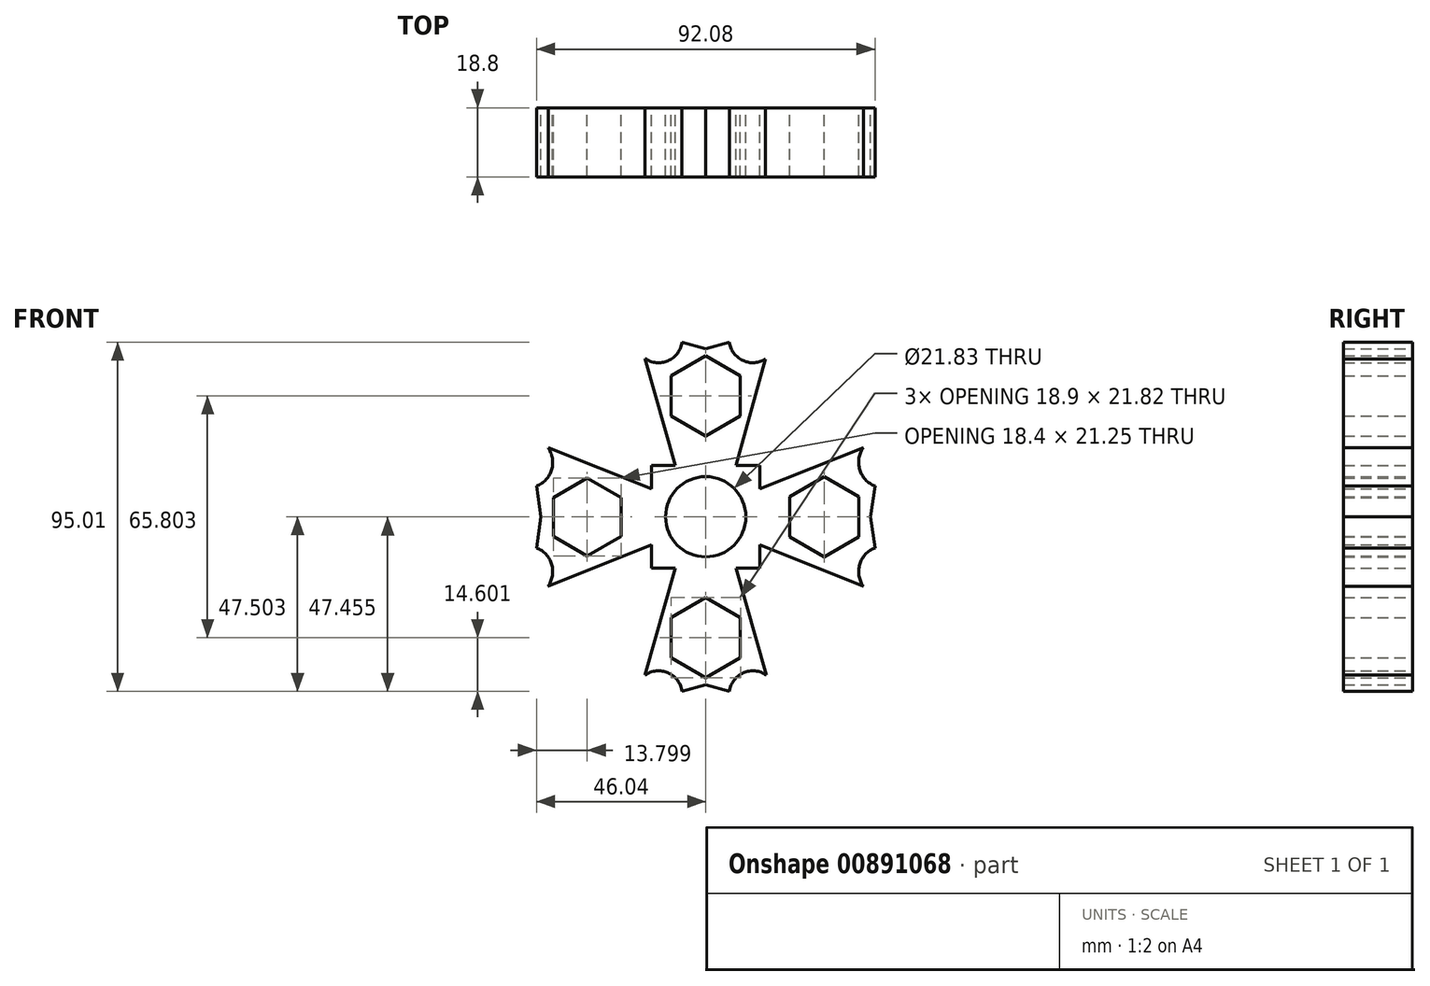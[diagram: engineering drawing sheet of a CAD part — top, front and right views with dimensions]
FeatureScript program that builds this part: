
annotation { "Feature Type Name" : "Feature", "Feature Type Description" : "" }
export const myFeature = defineFeature(function(context is Context, id is Id, definition is map)
    precondition{}
    {
        {
            var Q0;
            Q0=qCreatedBy(makeId("Front.planeOp"),FACE);
            var sketch = newSketch(context, id + "F0", { "sketchPlane" : qUnion([Q0])});
            skCircle(sketch, "E0", {"center": v(0, -32.8) * mm, "radius": 10.92 * mm});
            skLineSegment(sketch, "E1.bottom", {"start": v(-14.78, -18.87) * mm, "end": v(14.78, -18.87) * mm});
            skLineSegment(sketch, "E1.top", {"start": v(-14.78, -46.74) * mm, "end": v(14.78, -46.74) * mm});
            skLineSegment(sketch, "E1.left", {"start": v(-14.78, -18.87) * mm, "end": v(-14.78, -46.74) * mm});
            skLineSegment(sketch, "E1.right", {"start": v(14.78, -18.87) * mm, "end": v(14.78, -46.74) * mm});
            skLineSegment(sketch, "E2", {"start": v(-8.22, -18.87) * mm, "end": v(-16.53, 10.3) * mm});
            skLineSegment(sketch, "E3.MirrorCS", {"start": v(8.22, -18.87) * mm, "end": v(16.36, 10.35) * mm});
            skLineSegment(sketch, "E4.MirrorCS", {"start": v(-8.22, -46.74) * mm, "end": v(-16.53, -75.92) * mm});
            skLineSegment(sketch, "E5.MirrorCS", {"start": v(8.22, -46.74) * mm, "end": v(16.53, -75.92) * mm});
            skLineSegment(sketch, "E6.MirrorCS", {"start": v(-9.45, -60.25) * mm, "end": v(-9.45, -71.17) * mm});
            skPoint(sketch, "E7.MirrorP", {"position": v(-9.45, -65.7) * mm});
            skCircle(sketch, "E8.MirrorC", {"center": v(0, -65.7) * mm, "radius": 9.2 * mm, "construction": true});
            skLineSegment(sketch, "E9.MirrorCS", {"start": v(-9.45, -71.17) * mm, "end": v(0, -76.62) * mm});
            skLineSegment(sketch, "E10.MirrorCS", {"start": v(0, -76.62) * mm, "end": v(9.45, -71.17) * mm});
            skLineSegment(sketch, "E11.MirrorCS", {"start": v(9.45, -71.17) * mm, "end": v(9.45, -60.25) * mm});
            skLineSegment(sketch, "E12.MirrorCS", {"start": v(9.45, -60.25) * mm, "end": v(0, -54.8) * mm});
            skLineSegment(sketch, "E13.MirrorCS", {"start": v(0, -54.8) * mm, "end": v(-9.45, -60.25) * mm});
            skLineSegment(sketch, "E14", {"start": v(-14.78, -25.25) * mm, "end": v(-42.94, -13.95) * mm});
            skPoint(sketch, "E15.startSnap0", {"position": v(-14.78, -32.8) * mm});
            skLineSegment(sketch, "E16.MirrorCS", {"start": v(-14.73, -40.46) * mm, "end": v(-42.89, -51.76) * mm});
            skPoint(sketch, "E17.orphan", {"position": v(-58.79, -32.85) * mm});
            skPoint(sketch, "E18.orphan", {"position": v(-58.79, -32.8) * mm});
            skCircle(sketch, "E19.cCircle", {"center": v(-32.24, -32.85) * mm, "radius": 9.2 * mm, "construction": true});
            skLineSegment(sketch, "E19.0", {"start": v(-41.44, -38.17) * mm, "end": v(-41.44, -27.54) * mm});
            skLineSegment(sketch, "E19.1", {"start": v(-41.44, -27.54) * mm, "end": v(-32.24, -22.23) * mm});
            skLineSegment(sketch, "E19.2", {"start": v(-32.24, -22.23) * mm, "end": v(-23.04, -27.54) * mm});
            skLineSegment(sketch, "E19.3", {"start": v(-23.04, -27.54) * mm, "end": v(-23.04, -38.17) * mm});
            skLineSegment(sketch, "E19.4", {"start": v(-23.04, -38.17) * mm, "end": v(-32.24, -43.48) * mm});
            skLineSegment(sketch, "E19.5", {"start": v(-32.24, -43.48) * mm, "end": v(-41.44, -38.17) * mm});
            skPoint(sketch, "E19.0.midPoint", {"position": v(-41.44, -32.85) * mm});
            skLineSegment(sketch, "E20.MirrorCS", {"start": v(14.73, -25.25) * mm, "end": v(42.89, -13.95) * mm});
            skLineSegment(sketch, "E21.MirrorCS", {"start": v(14.73, -40.46) * mm, "end": v(42.89, -51.76) * mm});
            skLineSegment(sketch, "E22.MirrorCS", {"start": v(22.8, -38.31) * mm, "end": v(32.24, -43.77) * mm});
            skLineSegment(sketch, "E23.MirrorCS", {"start": v(22.8, -27.4) * mm, "end": v(22.8, -38.31) * mm});
            skCircle(sketch, "E24.MirrorC", {"center": v(32.24, -32.85) * mm, "radius": 9.2 * mm, "construction": true});
            skLineSegment(sketch, "E25.MirrorCS", {"start": v(32.24, -21.94) * mm, "end": v(22.8, -27.4) * mm});
            skLineSegment(sketch, "E26.MirrorCS", {"start": v(41.7, -27.4) * mm, "end": v(32.24, -21.94) * mm});
            skLineSegment(sketch, "E27.MirrorCS", {"start": v(41.7, -38.31) * mm, "end": v(41.7, -27.4) * mm});
            skLineSegment(sketch, "E28.MirrorCS", {"start": v(32.24, -43.77) * mm, "end": v(41.7, -38.31) * mm});
            skPoint(sketch, "E29.end.orphan", {"position": v(0, 28.84) * mm});
            skPoint(sketch, "E30.startSnap0", {"position": v(0, 21.1) * mm});
            skPoint(sketch, "E31.MirrorP", {"position": v(0, -86.81) * mm});
            skPoint(sketch, "E32.MirrorCS.end.orphan", {"position": v(4.4, 21.1) * mm});
            skPoint(sketch, "E33.start.orphan", {"position": v(-51.94, -27.4) * mm});
            skLineSegment(sketch, "E34", {"start": v(-14.78, -32.8) * mm, "end": v(14.78, -32.8) * mm, "construction": true});
            skLineSegment(sketch, "E35", {"start": v(0, -46.74) * mm, "end": v(0, -18.87) * mm, "construction": true});
            skLineSegment(sketch, "E36", {"start": v(-6.46, 14.7) * mm, "end": v(0, 12.96) * mm});
            skLineSegment(sketch, "E37.MirrorCS", {"start": v(6.46, 14.7) * mm, "end": v(0, 12.96) * mm});
            skArc(sketch, "E38.MirrorCS", {"start": v(16.53, 10.3) * mm, "mid": v(10.25, 9.65) * mm, "end": v(6.46, 14.7) * mm});
            skArc(sketch, "E39.MirrorCS", {"start": v(-16.53, -75.92) * mm, "mid": v(-10.25, -75.27) * mm, "end": v(-6.46, -80.31) * mm});
            skLineSegment(sketch, "E40.MirrorCS", {"start": v(-6.46, -80.31) * mm, "end": v(0, -78.57) * mm});
            skLineSegment(sketch, "E41.MirrorCS", {"start": v(6.46, -80.31) * mm, "end": v(0, -78.57) * mm});
            skArc(sketch, "E42.MirrorCS", {"start": v(16.53, -75.92) * mm, "mid": v(10.25, -75.27) * mm, "end": v(6.46, -80.31) * mm});
            skArc(sketch, "E43", {"start": v(-42.89, -51.76) * mm, "mid": v(-41.9, -45.74) * mm, "end": v(-46.04, -41.26) * mm});
            skLineSegment(sketch, "E44", {"start": v(-46.04, -41.26) * mm, "end": v(-44.8, -32.85) * mm});
            skLineSegment(sketch, "E45.MirrorCS", {"start": v(-46.04, -24.45) * mm, "end": v(-44.8, -32.85) * mm});
            skArc(sketch, "E46.MirrorCS", {"start": v(-42.89, -13.95) * mm, "mid": v(-41.9, -19.97) * mm, "end": v(-46.04, -24.45) * mm});
            skArc(sketch, "E47.MirrorCS", {"start": v(42.89, -51.76) * mm, "mid": v(41.9, -45.74) * mm, "end": v(46.04, -41.26) * mm});
            skLineSegment(sketch, "E48.MirrorCS", {"start": v(46.04, -41.26) * mm, "end": v(44.8, -32.85) * mm});
            skLineSegment(sketch, "E49.MirrorCS", {"start": v(46.04, -24.45) * mm, "end": v(44.8, -32.85) * mm});
            skArc(sketch, "E50.MirrorCS", {"start": v(42.89, -13.95) * mm, "mid": v(41.9, -19.97) * mm, "end": v(46.04, -24.45) * mm});
            skArc(sketch, "E51.MirrorCS", {"start": v(-16.53, 10.3) * mm, "mid": v(-10.25, 9.65) * mm, "end": v(-6.46, 14.7) * mm});
            skCircle(sketch, "E52.MirrorC", {"center": v(0, 0.1) * mm, "radius": 9.2 * mm, "construction": true});
            skLineSegment(sketch, "E53.MirrorCS", {"start": v(0, -10.82) * mm, "end": v(-9.45, -5.36) * mm});
            skLineSegment(sketch, "E54.MirrorCS", {"start": v(9.45, -5.36) * mm, "end": v(0, -10.82) * mm});
            skLineSegment(sketch, "E55.MirrorCS", {"start": v(9.45, 5.55) * mm, "end": v(9.45, -5.36) * mm});
            skLineSegment(sketch, "E56.MirrorCS", {"start": v(0, 11) * mm, "end": v(9.45, 5.55) * mm});
            skLineSegment(sketch, "E57.MirrorCS", {"start": v(-9.45, 5.55) * mm, "end": v(0, 11) * mm});
            skLineSegment(sketch, "E58.MirrorCS", {"start": v(-9.45, -5.36) * mm, "end": v(-9.45, 5.55) * mm});
            skSolve(sketch);
        }
        {
            var Q0;
            Q0 = qSketchRegion(id + "F0", true);
            extrude(context, id + "F1", {"entities" : qUnion([Q0]), "depth" : 18.8 * mm, "offsetDistance" : 25 * mm});
        }
    });
